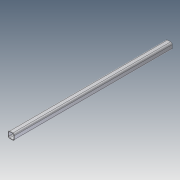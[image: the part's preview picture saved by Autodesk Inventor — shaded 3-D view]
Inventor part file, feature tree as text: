
AUTODESK INVENTOR PART (.ipt)
format: ipt  version: unknown  size: 178,688 bytes
history: native  units: in
note: dims shown in document units (in); Inventor stores cm internally (conversion verified against a paired STEP export)
features: extrude x1, sketch x1
ambient origin geometry x8: Origin, YZ Plane, XZ Plane, XY Plane, X Axis, Y Axis, Z Axis, Center Point
bodies: Solid1 (feature_tree)
feature tree (2):
  extrude  "Extrusion1"  Depth=0.375in
  sketch  "Sketch1"  dims[d0=1.5in d1=0.375in d2=0.125in d3=37.0in d4=0.0in]
